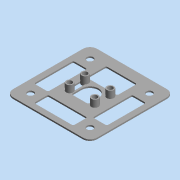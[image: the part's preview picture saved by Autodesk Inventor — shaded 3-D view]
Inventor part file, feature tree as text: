
AUTODESK INVENTOR PART (.ipt)
format: ipt  version: 2015 (Build 190159000, 159)  size: 193,024 bytes
history: native  units: mm (DEFAULTED — no unit token found)
features: extrude x2, fillet x2
ambient origin geometry x8: Origin, YZ Plane, XZ Plane, XY Plane, X Axis, Y Axis, Z Axis, Center Point
bodies: Solid1 (feature_tree)
feature tree (4):
  extrude  "Extrusion1"  Depth=4.5mm
  extrude  "Extrusion2"  Depth=4.5mm
  fillet  "Fillet1"  Radius=4.5mm
  fillet  "Fillet2"  Radius=4.5mm
